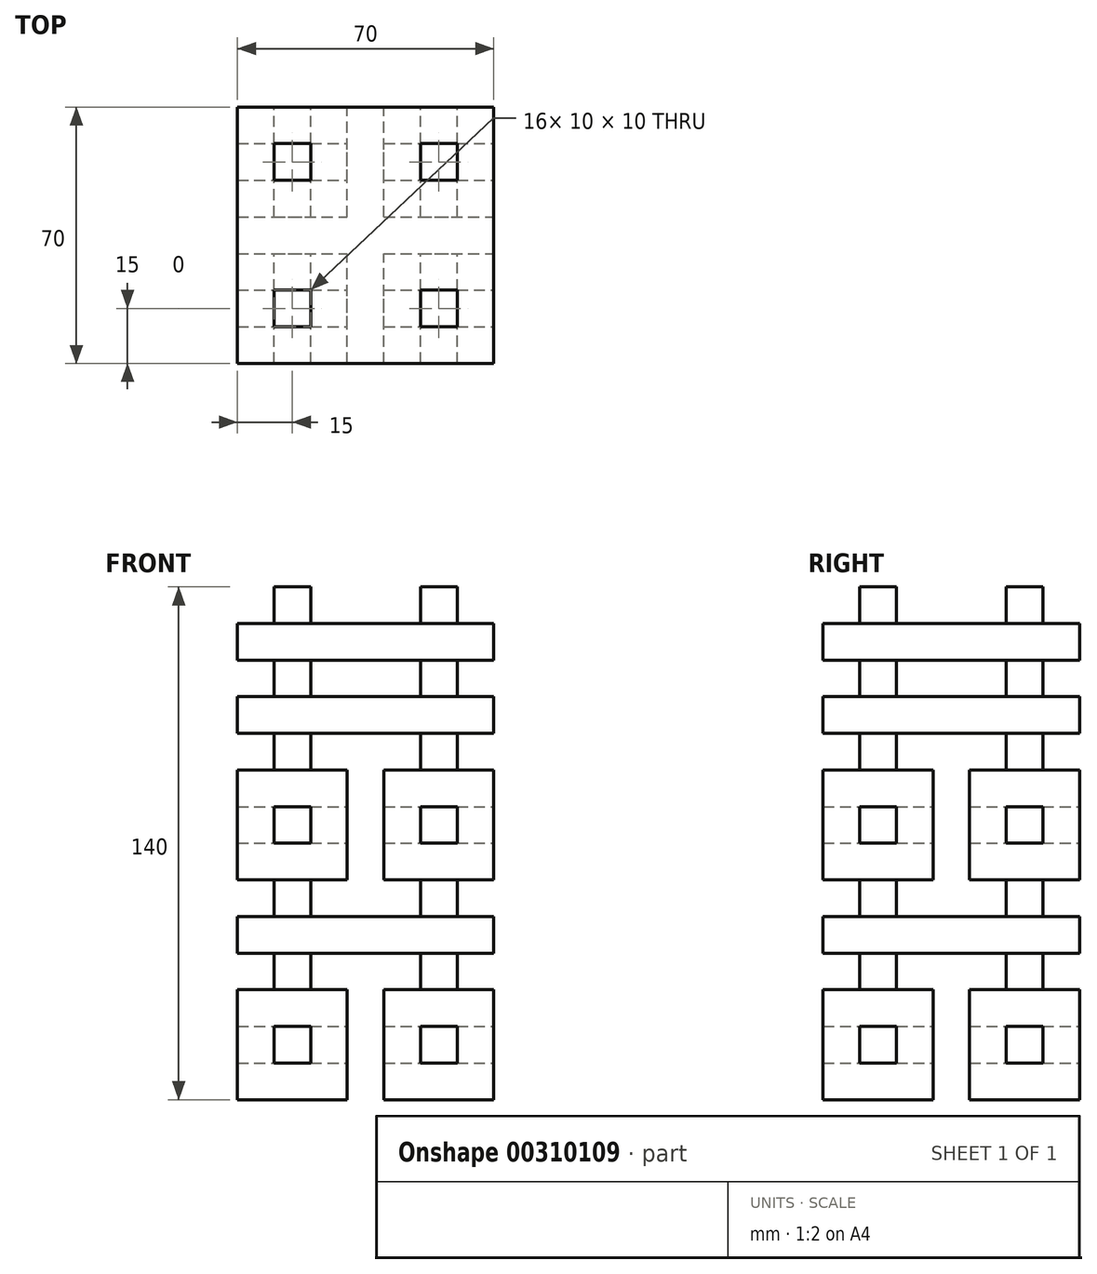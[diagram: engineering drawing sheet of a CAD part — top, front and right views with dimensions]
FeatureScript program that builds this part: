
annotation { "Feature Type Name" : "Feature", "Feature Type Description" : "" }
export const myFeature = defineFeature(function(context is Context, id is Id, definition is map)
    precondition{}
    {
        {
            var Q0;
            Q0=qCreatedBy(makeId("Front.planeOp"),FACE);
            var sketch = newSketch(context, id + "F0", { "sketchPlane" : qUnion([Q0])});
            skLineSegment(sketch, "E0.bottom", {"start": v(-25, 70) * mm, "end": v(-15, 70) * mm});
            skLineSegment(sketch, "E0.top", {"start": v(-35, -70) * mm, "end": v(-5, -70) * mm});
            skLineSegment(sketch, "E0.left", {"start": v(-35, 60) * mm, "end": v(-35, 50) * mm});
            skLineSegment(sketch, "E0.right", {"start": v(35, 60) * mm, "end": v(35, 50) * mm});
            skPoint(sketch, "E0.middle", {"position": v(0, 0) * mm});
            skLineSegment(sketch, "E1", {"start": v(-35, 60) * mm, "end": v(-25, 60) * mm});
            skLineSegment(sketch, "E2", {"start": v(-35, 50) * mm, "end": v(-25, 50) * mm});
            skLineSegment(sketch, "E3", {"start": v(-35, 40) * mm, "end": v(-25, 40) * mm});
            skLineSegment(sketch, "E4", {"start": v(-35, 20) * mm, "end": v(-25, 20) * mm});
            skLineSegment(sketch, "E5", {"start": v(-25, 10) * mm, "end": v(-15, 10) * mm});
            skLineSegment(sketch, "E6", {"start": v(-25, 0) * mm, "end": v(-15, 0) * mm});
            skLineSegment(sketch, "E7", {"start": v(-35, -10) * mm, "end": v(-25, -10) * mm});
            skLineSegment(sketch, "E8", {"start": v(-35, -20) * mm, "end": v(-25, -20) * mm});
            skLineSegment(sketch, "E9", {"start": v(-35, -30) * mm, "end": v(-25, -30) * mm});
            skLineSegment(sketch, "E10", {"start": v(-35, -40) * mm, "end": v(-25, -40) * mm});
            skLineSegment(sketch, "E11", {"start": v(-25, -50) * mm, "end": v(-15, -50) * mm});
            skLineSegment(sketch, "E12", {"start": v(-25, -60) * mm, "end": v(-15, -60) * mm});
            skLineSegment(sketch, "E13", {"start": v(-35, 30) * mm, "end": v(-25, 30) * mm});
            skLineSegment(sketch, "E14", {"start": v(-25, 70) * mm, "end": v(-25, 60) * mm});
            skLineSegment(sketch, "E15", {"start": v(-15, 70) * mm, "end": v(-15, 60) * mm});
            skLineSegment(sketch, "E16", {"start": v(-5, 20) * mm, "end": v(-5, -10) * mm});
            skLineSegment(sketch, "E17", {"start": v(5, 20) * mm, "end": v(5, -10) * mm});
            skLineSegment(sketch, "E18", {"start": v(15, 70) * mm, "end": v(15, 60) * mm});
            skLineSegment(sketch, "E19", {"start": v(25, 70) * mm, "end": v(25, 60) * mm});
            skPoint(sketch, "E20.orphan", {"position": v(-35, 70) * mm});
            skLineSegment(sketch, "E21.trimOffspring", {"start": v(-35, 40) * mm, "end": v(-35, 30) * mm});
            skLineSegment(sketch, "E22.trimOffspring", {"start": v(15, 70) * mm, "end": v(25, 70) * mm});
            skPoint(sketch, "E23.orphan", {"position": v(-5, 70) * mm});
            skPoint(sketch, "E24.orphan", {"position": v(5, 70) * mm});
            skPoint(sketch, "E25.orphan", {"position": v(35, 70) * mm});
            skLineSegment(sketch, "E26.trimOffspring", {"start": v(-25, 50) * mm, "end": v(-25, 40) * mm});
            skLineSegment(sketch, "E27.trimOffspring", {"start": v(-15, 50) * mm, "end": v(-15, 40) * mm});
            skLineSegment(sketch, "E28.trimOffspring", {"start": v(15, 50) * mm, "end": v(15, 40) * mm});
            skLineSegment(sketch, "E29.trimOffspring", {"start": v(25, 50) * mm, "end": v(25, 40) * mm});
            skLineSegment(sketch, "E30.trimOffspring", {"start": v(-15, 60) * mm, "end": v(15, 60) * mm});
            skLineSegment(sketch, "E31.trimOffspring", {"start": v(25, 60) * mm, "end": v(35, 60) * mm});
            skLineSegment(sketch, "E32.trimOffspring", {"start": v(-15, 50) * mm, "end": v(15, 50) * mm});
            skLineSegment(sketch, "E33.trimOffspring", {"start": v(25, 50) * mm, "end": v(35, 50) * mm});
            skLineSegment(sketch, "E34.trimOffspring", {"start": v(-15, 40) * mm, "end": v(15, 40) * mm});
            skLineSegment(sketch, "E35.trimOffspring", {"start": v(25, 40) * mm, "end": v(35, 40) * mm});
            skLineSegment(sketch, "E36.trimOffspring", {"start": v(-25, 30) * mm, "end": v(-25, 20) * mm});
            skLineSegment(sketch, "E37.trimOffspring", {"start": v(-15, 30) * mm, "end": v(-15, 20) * mm});
            skLineSegment(sketch, "E38.trimOffspring", {"start": v(15, 30) * mm, "end": v(15, 20) * mm});
            skLineSegment(sketch, "E39.trimOffspring", {"start": v(25, 30) * mm, "end": v(25, 20) * mm});
            skLineSegment(sketch, "E40.trimOffspring", {"start": v(-35, 20) * mm, "end": v(-35, -10) * mm});
            skLineSegment(sketch, "E41.trimOffspring", {"start": v(-15, 30) * mm, "end": v(15, 30) * mm});
            skLineSegment(sketch, "E42.trimOffspring", {"start": v(25, 30) * mm, "end": v(35, 30) * mm});
            skLineSegment(sketch, "E43.trimOffspring", {"start": v(35, 20) * mm, "end": v(35, -10) * mm});
            skLineSegment(sketch, "E44.trimOffspring", {"start": v(-15, 20) * mm, "end": v(-5, 20) * mm});
            skLineSegment(sketch, "E45.trimOffspring", {"start": v(25, 20) * mm, "end": v(35, 20) * mm});
            skLineSegment(sketch, "E46.trimOffspring", {"start": v(-25, 10) * mm, "end": v(-25, 0) * mm});
            skLineSegment(sketch, "E47.trimOffspring", {"start": v(-15, 10) * mm, "end": v(-15, 0) * mm});
            skLineSegment(sketch, "E48.trimOffspring", {"start": v(15, 10) * mm, "end": v(25, 10) * mm});
            skPoint(sketch, "E49.orphan", {"position": v(-35, 10) * mm});
            skPoint(sketch, "E50.orphan", {"position": v(-35, 0) * mm});
            skLineSegment(sketch, "E51.trimOffspring", {"start": v(-25, -10) * mm, "end": v(-25, -20) * mm});
            skLineSegment(sketch, "E52.trimOffspring", {"start": v(-15, -10) * mm, "end": v(-15, -20) * mm});
            skLineSegment(sketch, "E53.trimOffspring", {"start": v(5, 20) * mm, "end": v(15, 20) * mm});
            skLineSegment(sketch, "E54.trimOffspring", {"start": v(15, 0) * mm, "end": v(25, 0) * mm});
            skLineSegment(sketch, "E55.trimOffspring", {"start": v(5, -10) * mm, "end": v(15, -10) * mm});
            skLineSegment(sketch, "E56.trimOffspring", {"start": v(25, 10) * mm, "end": v(25, 0) * mm});
            skLineSegment(sketch, "E57.trimOffspring", {"start": v(15, 10) * mm, "end": v(15, 0) * mm});
            skLineSegment(sketch, "E58.trimOffspring", {"start": v(15, -10) * mm, "end": v(15, -20) * mm});
            skLineSegment(sketch, "E59.trimOffspring", {"start": v(25, -10) * mm, "end": v(25, -20) * mm});
            skLineSegment(sketch, "E60.trimOffspring", {"start": v(-35, -20) * mm, "end": v(-35, -30) * mm});
            skLineSegment(sketch, "E61.trimOffspring", {"start": v(-5, -40) * mm, "end": v(-5, -70) * mm});
            skLineSegment(sketch, "E62.trimOffspring", {"start": v(-15, -10) * mm, "end": v(-5, -10) * mm});
            skLineSegment(sketch, "E63.trimOffspring", {"start": v(25, -10) * mm, "end": v(35, -10) * mm});
            skLineSegment(sketch, "E64.trimOffspring", {"start": v(5, -40) * mm, "end": v(5, -70) * mm});
            skLineSegment(sketch, "E65.trimOffspring", {"start": v(35, -20) * mm, "end": v(35, -30) * mm});
            skLineSegment(sketch, "E66.trimOffspring", {"start": v(-15, -20) * mm, "end": v(15, -20) * mm});
            skLineSegment(sketch, "E67.trimOffspring", {"start": v(25, -20) * mm, "end": v(35, -20) * mm});
            skLineSegment(sketch, "E68.trimOffspring", {"start": v(-35, -40) * mm, "end": v(-35, -70) * mm});
            skLineSegment(sketch, "E69.trimOffspring", {"start": v(-25, -30) * mm, "end": v(-25, -40) * mm});
            skLineSegment(sketch, "E70.trimOffspring", {"start": v(-15, -30) * mm, "end": v(-15, -40) * mm});
            skLineSegment(sketch, "E71.trimOffspring", {"start": v(15, -30) * mm, "end": v(15, -40) * mm});
            skLineSegment(sketch, "E72.trimOffspring", {"start": v(25, -30) * mm, "end": v(25, -40) * mm});
            skLineSegment(sketch, "E73.trimOffspring", {"start": v(35, 40) * mm, "end": v(35, 30) * mm});
            skLineSegment(sketch, "E74.trimOffspring", {"start": v(35, -40) * mm, "end": v(35, -70) * mm});
            skLineSegment(sketch, "E75.trimOffspring", {"start": v(5, -40) * mm, "end": v(15, -40) * mm});
            skLineSegment(sketch, "E76.trimOffspring", {"start": v(15, -50) * mm, "end": v(25, -50) * mm});
            skLineSegment(sketch, "E77.trimOffspring", {"start": v(15, -60) * mm, "end": v(25, -60) * mm});
            skLineSegment(sketch, "E78.trimOffspring", {"start": v(5, -70) * mm, "end": v(35, -70) * mm});
            skLineSegment(sketch, "E79.trimOffspring", {"start": v(-25, -50) * mm, "end": v(-25, -60) * mm});
            skLineSegment(sketch, "E80.trimOffspring", {"start": v(-15, -50) * mm, "end": v(-15, -60) * mm});
            skPoint(sketch, "E81.orphan", {"position": v(-35, -60) * mm});
            skPoint(sketch, "E82.orphan", {"position": v(-35, -50) * mm});
            skLineSegment(sketch, "E83.trimOffspring", {"start": v(25, -50) * mm, "end": v(25, -60) * mm});
            skLineSegment(sketch, "E84.trimOffspring", {"start": v(15, -50) * mm, "end": v(15, -60) * mm});
            skLineSegment(sketch, "E85.trimOffspring", {"start": v(25, -40) * mm, "end": v(35, -40) * mm});
            skLineSegment(sketch, "E86.trimOffspring", {"start": v(-15, -40) * mm, "end": v(-5, -40) * mm});
            skLineSegment(sketch, "E87.trimOffspring", {"start": v(-15, -30) * mm, "end": v(15, -30) * mm});
            skLineSegment(sketch, "E88.trimOffspring", {"start": v(25, -30) * mm, "end": v(35, -30) * mm});
            skSolve(sketch);
        }
        {
            var Q0;
            Q0 = qSketchRegion(id + "F0", true);
            extrude(context, id + "F1", {"entities" : qUnion([Q0]), "depth" : 70 * mm});
        }
        {
            var Q0;
            Q0=makeQuery(id+"F1.opExtrude","SWEPT_FACE",FACE,{"disambiguationData":[OSD([sQuery(id+"F0.wireOp",EDGE,"E74.trimOffspring")])]});
            var sketch = newSketch(context, id + "F2", { "sketchPlane" : qUnion([Q0])});
            skLineSegment(sketch, "E89", {"start": v(-70, 70) * mm, "end": v(-60, 70) * mm});
            skLineSegment(sketch, "E90", {"start": v(0, 70) * mm, "end": v(0, 60) * mm});
            skLineSegment(sketch, "E91", {"start": v(-30, -70) * mm, "end": v(-40, -70) * mm});
            skLineSegment(sketch, "E92", {"start": v(0, 60) * mm, "end": v(-10, 60) * mm});
            skLineSegment(sketch, "E93", {"start": v(0, 50) * mm, "end": v(-10, 50) * mm});
            skLineSegment(sketch, "E94", {"start": v(-70, 40) * mm, "end": v(-60, 40) * mm});
            skLineSegment(sketch, "E95", {"start": v(-70, 30) * mm, "end": v(-60, 30) * mm});
            skLineSegment(sketch, "E96", {"start": v(-70, 20) * mm, "end": v(-60, 20) * mm});
            skLineSegment(sketch, "E97", {"start": v(-60, 10) * mm, "end": v(-50, 10) * mm});
            skLineSegment(sketch, "E98", {"start": v(-70, -20) * mm, "end": v(-60, -20) * mm});
            skLineSegment(sketch, "E99", {"start": v(-70, -30) * mm, "end": v(-60, -30) * mm});
            skLineSegment(sketch, "E100", {"start": v(-70, -40) * mm, "end": v(-60, -40) * mm});
            skLineSegment(sketch, "E101", {"start": v(-60, 70) * mm, "end": v(-60, 60) * mm});
            skLineSegment(sketch, "E102", {"start": v(-50, 70) * mm, "end": v(-50, 60) * mm});
            skLineSegment(sketch, "E103", {"start": v(-20, 70) * mm, "end": v(-20, 60) * mm});
            skLineSegment(sketch, "E104", {"start": v(-10, 70) * mm, "end": v(-10, 60) * mm});
            skLineSegment(sketch, "E105", {"start": v(-60, 0) * mm, "end": v(-50, 0) * mm});
            skLineSegment(sketch, "E106", {"start": v(-60, -50) * mm, "end": v(-50, -50) * mm});
            skLineSegment(sketch, "E107", {"start": v(-60, -60) * mm, "end": v(-50, -60) * mm});
            skLineSegment(sketch, "E108", {"start": v(-70, -10) * mm, "end": v(-60, -10) * mm});
            skLineSegment(sketch, "E109.trimOffspring", {"start": v(-50, 70) * mm, "end": v(-20, 70) * mm});
            skLineSegment(sketch, "E110.trimOffspring", {"start": v(-70, 60) * mm, "end": v(-70, 70) * mm});
            skLineSegment(sketch, "E111.trimOffspring", {"start": v(-60, 50) * mm, "end": v(-60, 40) * mm});
            skLineSegment(sketch, "E112.trimOffspring", {"start": v(-50, 50) * mm, "end": v(-50, 40) * mm});
            skLineSegment(sketch, "E113.trimOffspring", {"start": v(-20, 50) * mm, "end": v(-20, 40) * mm});
            skLineSegment(sketch, "E114.trimOffspring", {"start": v(-10, 50) * mm, "end": v(-10, 40) * mm});
            skLineSegment(sketch, "E115.trimOffspring", {"start": v(0, 50) * mm, "end": v(0, 40) * mm});
            skLineSegment(sketch, "E116.trimOffspring", {"start": v(-60, 60) * mm, "end": v(-70, 60) * mm});
            skLineSegment(sketch, "E117.trimOffspring", {"start": v(-10, 70) * mm, "end": v(0, 70) * mm});
            skLineSegment(sketch, "E118.trimOffspring", {"start": v(-20, 60) * mm, "end": v(-50, 60) * mm});
            skPoint(sketch, "E119.start.orphan", {"position": v(-40, 70) * mm});
            skPoint(sketch, "E120.start.orphan", {"position": v(-30, 70) * mm});
            skLineSegment(sketch, "E121.trimOffspring", {"start": v(-60, 50) * mm, "end": v(-70, 50) * mm});
            skLineSegment(sketch, "E122.trimOffspring", {"start": v(-50, 40) * mm, "end": v(-20, 40) * mm});
            skLineSegment(sketch, "E123.trimOffspring", {"start": v(-70, 40) * mm, "end": v(-70, 50) * mm});
            skLineSegment(sketch, "E124.trimOffspring", {"start": v(-60, 30) * mm, "end": v(-60, 20) * mm});
            skLineSegment(sketch, "E125.trimOffspring", {"start": v(-50, 30) * mm, "end": v(-50, 20) * mm});
            skLineSegment(sketch, "E126.trimOffspring", {"start": v(-40, 20) * mm, "end": v(-40, -10) * mm});
            skLineSegment(sketch, "E127.trimOffspring", {"start": v(-30, 20) * mm, "end": v(-30, -10) * mm});
            skLineSegment(sketch, "E128.trimOffspring", {"start": v(-20, 30) * mm, "end": v(-20, 20) * mm});
            skLineSegment(sketch, "E129.trimOffspring", {"start": v(-10, 30) * mm, "end": v(-10, 20) * mm});
            skLineSegment(sketch, "E130.trimOffspring", {"start": v(0, 30) * mm, "end": v(0, 20) * mm});
            skLineSegment(sketch, "E131.trimOffspring", {"start": v(-20, 50) * mm, "end": v(-50, 50) * mm});
            skLineSegment(sketch, "E132.trimOffspring", {"start": v(-10, 40) * mm, "end": v(0, 40) * mm});
            skLineSegment(sketch, "E133.trimOffspring", {"start": v(-50, 30) * mm, "end": v(-20, 30) * mm});
            skLineSegment(sketch, "E134.trimOffspring", {"start": v(-50, 20) * mm, "end": v(-40, 20) * mm});
            skLineSegment(sketch, "E135.trimOffspring", {"start": v(-70, 20) * mm, "end": v(-70, 30) * mm});
            skLineSegment(sketch, "E136.trimOffspring", {"start": v(-10, 30) * mm, "end": v(0, 30) * mm});
            skLineSegment(sketch, "E137.trimOffspring", {"start": v(-10, 20) * mm, "end": v(0, 20) * mm});
            skLineSegment(sketch, "E138.trimOffspring", {"start": v(-60, 10) * mm, "end": v(-60, 0) * mm});
            skLineSegment(sketch, "E139.trimOffspring", {"start": v(-50, 10) * mm, "end": v(-50, 0) * mm});
            skLineSegment(sketch, "E140.trimOffspring", {"start": v(-30, 20) * mm, "end": v(-20, 20) * mm});
            skLineSegment(sketch, "E141.trimOffspring", {"start": v(-20, 10) * mm, "end": v(-20, 0) * mm});
            skLineSegment(sketch, "E142.trimOffspring", {"start": v(-10, 10) * mm, "end": v(-10, 0) * mm});
            skLineSegment(sketch, "E143.trimOffspring", {"start": v(-20, 10) * mm, "end": v(-10, 10) * mm});
            skLineSegment(sketch, "E144.trimOffspring", {"start": v(-20, 0) * mm, "end": v(-10, 0) * mm});
            skLineSegment(sketch, "E145.trimOffspring", {"start": v(-50, -10) * mm, "end": v(-50, -20) * mm});
            skLineSegment(sketch, "E146.trimOffspring", {"start": v(-60, -10) * mm, "end": v(-60, -20) * mm});
            skPoint(sketch, "E147.orphan", {"position": v(-70, 10) * mm});
            skPoint(sketch, "E148.orphan", {"position": v(-70, 0) * mm});
            skLineSegment(sketch, "E149.trimOffspring", {"start": v(-20, -10) * mm, "end": v(-20, -20) * mm});
            skLineSegment(sketch, "E150.trimOffspring", {"start": v(-10, -10) * mm, "end": v(-10, -20) * mm});
            skLineSegment(sketch, "E151.trimOffspring", {"start": v(0, -10) * mm, "end": v(0, -20) * mm});
            skLineSegment(sketch, "E152.trimOffspring", {"start": v(-50, -10) * mm, "end": v(-40, -10) * mm});
            skLineSegment(sketch, "E153.trimOffspring", {"start": v(-50, -20) * mm, "end": v(-20, -20) * mm});
            skLineSegment(sketch, "E154.trimOffspring", {"start": v(-30, -10) * mm, "end": v(-20, -10) * mm});
            skLineSegment(sketch, "E155.trimOffspring", {"start": v(-40, -40) * mm, "end": v(-40, -70) * mm});
            skLineSegment(sketch, "E156.trimOffspring", {"start": v(-30, -40) * mm, "end": v(-30, -70) * mm});
            skLineSegment(sketch, "E157.trimOffspring", {"start": v(-10, -10) * mm, "end": v(0, -10) * mm});
            skLineSegment(sketch, "E158.trimOffspring", {"start": v(-10, -20) * mm, "end": v(0, -20) * mm});
            skLineSegment(sketch, "E159.trimOffspring", {"start": v(-70, -20) * mm, "end": v(-70, -10) * mm});
            skLineSegment(sketch, "E160.trimOffspring", {"start": v(-60, -30) * mm, "end": v(-60, -40) * mm});
            skLineSegment(sketch, "E161.trimOffspring", {"start": v(-50, -30) * mm, "end": v(-50, -40) * mm});
            skLineSegment(sketch, "E162.trimOffspring", {"start": v(-20, -30) * mm, "end": v(-20, -40) * mm});
            skLineSegment(sketch, "E163.trimOffspring", {"start": v(-10, -30) * mm, "end": v(-10, -40) * mm});
            skLineSegment(sketch, "E164.trimOffspring", {"start": v(0, -30) * mm, "end": v(0, -40) * mm});
            skLineSegment(sketch, "E165.trimOffspring", {"start": v(-50, -30) * mm, "end": v(-20, -30) * mm});
            skLineSegment(sketch, "E166.trimOffspring", {"start": v(-50, -40) * mm, "end": v(-40, -40) * mm});
            skLineSegment(sketch, "E167.trimOffspring", {"start": v(-60, -50) * mm, "end": v(-60, -60) * mm});
            skLineSegment(sketch, "E168.trimOffspring", {"start": v(-70, -40) * mm, "end": v(-70, -30) * mm});
            skPoint(sketch, "E169.orphan", {"position": v(-70, -50) * mm});
            skPoint(sketch, "E170.end.orphan", {"position": v(-70, -60) * mm});
            skPoint(sketch, "E171.orphan", {"position": v(-70, -70) * mm});
            skLineSegment(sketch, "E172.trimOffspring", {"start": v(-50, -50) * mm, "end": v(-50, -60) * mm});
            skLineSegment(sketch, "E173.trimOffspring", {"start": v(-10, -50) * mm, "end": v(-10, -60) * mm});
            skLineSegment(sketch, "E174.trimOffspring", {"start": v(-20, -50) * mm, "end": v(-20, -60) * mm});
            skLineSegment(sketch, "E175.trimOffspring", {"start": v(-20, -50) * mm, "end": v(-10, -50) * mm});
            skLineSegment(sketch, "E176.trimOffspring", {"start": v(-20, -60) * mm, "end": v(-10, -60) * mm});
            skPoint(sketch, "E177.orphan", {"position": v(0, -50) * mm});
            skPoint(sketch, "E178.orphan", {"position": v(0, -60) * mm});
            skLineSegment(sketch, "E179.trimOffspring", {"start": v(-30, -40) * mm, "end": v(-20, -40) * mm});
            skLineSegment(sketch, "E180.trimOffspring", {"start": v(-10, -40) * mm, "end": v(0, -40) * mm});
            skLineSegment(sketch, "E181.trimOffspring", {"start": v(-10, -30) * mm, "end": v(0, -30) * mm});
            skSolve(sketch);
        }
        {
            var Q0;
            Q0=makeQuery(id+"F2.imprint","IMPRINT",FACE,{"disambiguationData":[TD([[makeQuery(id+"F2.imprint","IMPRINT",EDGE,{"derivedFrom":sQuery(id+"F2.wireOp",EDGE,"E125.trimOffspring")}),1.0]])]});
            var Q1;
            Q1=makeQuery(id+"F2.imprint","IMPRINT",FACE,{"disambiguationData":[TD([[makeQuery(id+"F2.imprint","IMPRINT",EDGE,{"derivedFrom":sQuery(id+"F2.wireOp",EDGE,"E150.trimOffspring")}),1.0]])]});
            var Q2;
            Q2=makeQuery(id+"F2.imprint","IMPRINT",FACE,{"disambiguationData":[TD([[makeQuery(id+"F2.imprint","IMPRINT",EDGE,{"derivedFrom":sQuery(id+"F2.wireOp",EDGE,"E141.trimOffspring")}),1.0]])]});
            var Q3;
            Q3=makeQuery(id+"F2.imprint","IMPRINT",FACE,{"disambiguationData":[TD([[makeQuery(id+"F2.imprint","IMPRINT",EDGE,{"derivedFrom":sQuery(id+"F2.wireOp",EDGE,"E97")}),-1.0]])]});
            var Q4;
            Q4=makeQuery(id+"F2.imprint","IMPRINT",FACE,{"disambiguationData":[TD([[makeQuery(id+"F2.imprint","IMPRINT",EDGE,{"derivedFrom":sQuery(id+"F2.wireOp",EDGE,"E95")}),-1.0]])]});
            var Q5;
            Q5=makeQuery(id+"F2.imprint","IMPRINT",FACE,{"disambiguationData":[TD([[makeQuery(id+"F2.imprint","IMPRINT",EDGE,{"derivedFrom":sQuery(id+"F2.wireOp",EDGE,"E129.trimOffspring")}),1.0]])]});
            var Q6;
            Q6=makeQuery(id+"F2.imprint","IMPRINT",FACE,{"disambiguationData":[TD([[makeQuery(id+"F2.imprint","IMPRINT",EDGE,{"derivedFrom":sQuery(id+"F2.wireOp",EDGE,"E93")}),1.0]])]});
            var Q7;
            Q7=makeQuery(id+"F2.imprint","IMPRINT",FACE,{"disambiguationData":[TD([[makeQuery(id+"F2.imprint","IMPRINT",EDGE,{"derivedFrom":sQuery(id+"F2.wireOp",EDGE,"E112.trimOffspring")}),1.0]])]});
            var Q8;
            Q8=makeQuery(id+"F2.imprint","IMPRINT",FACE,{"disambiguationData":[TD([[makeQuery(id+"F2.imprint","IMPRINT",EDGE,{"derivedFrom":sQuery(id+"F2.wireOp",EDGE,"E94")}),1.0]])]});
            var Q9;
            Q9=makeQuery(id+"F2.imprint","IMPRINT",FACE,{"disambiguationData":[TD([[makeQuery(id+"F2.imprint","IMPRINT",EDGE,{"derivedFrom":sQuery(id+"F2.wireOp",EDGE,"E89")}),-1.0]])]});
            var Q10;
            Q10=makeQuery(id+"F2.imprint","IMPRINT",FACE,{"disambiguationData":[TD([[makeQuery(id+"F2.imprint","IMPRINT",EDGE,{"derivedFrom":sQuery(id+"F2.wireOp",EDGE,"E102")}),1.0]])]});
            var Q11;
            Q11=makeQuery(id+"F2.imprint","IMPRINT",FACE,{"disambiguationData":[TD([[makeQuery(id+"F2.imprint","IMPRINT",EDGE,{"derivedFrom":sQuery(id+"F2.wireOp",EDGE,"E90")}),-1.0]])]});
            var Q12;
            Q12=makeQuery(id+"F2.imprint","IMPRINT",FACE,{"disambiguationData":[TD([[makeQuery(id+"F2.imprint","IMPRINT",EDGE,{"derivedFrom":sQuery(id+"F2.wireOp",EDGE,"E98")}),1.0]])]});
            var Q13;
            Q13=makeQuery(id+"F2.imprint","IMPRINT",FACE,{"disambiguationData":[TD([[makeQuery(id+"F2.imprint","IMPRINT",EDGE,{"derivedFrom":sQuery(id+"F2.wireOp",EDGE,"E99")}),-1.0]])]});
            var Q14;
            Q14=makeQuery(id+"F2.imprint","IMPRINT",FACE,{"disambiguationData":[TD([[makeQuery(id+"F2.imprint","IMPRINT",EDGE,{"derivedFrom":sQuery(id+"F2.wireOp",EDGE,"E161.trimOffspring")}),1.0]])]});
            var Q15;
            Q15=makeQuery(id+"F2.imprint","IMPRINT",FACE,{"disambiguationData":[TD([[makeQuery(id+"F2.imprint","IMPRINT",EDGE,{"derivedFrom":sQuery(id+"F2.wireOp",EDGE,"E163.trimOffspring")}),1.0]])]});
            var Q16;
            Q16=makeQuery(id+"F2.imprint","IMPRINT",FACE,{"disambiguationData":[TD([[makeQuery(id+"F2.imprint","IMPRINT",EDGE,{"derivedFrom":sQuery(id+"F2.wireOp",EDGE,"E173.trimOffspring")}),-1.0]])]});
            var Q17;
            Q17=makeQuery(id+"F2.imprint","IMPRINT",FACE,{"disambiguationData":[TD([[makeQuery(id+"F2.imprint","IMPRINT",EDGE,{"derivedFrom":sQuery(id+"F2.wireOp",EDGE,"E106")}),-1.0]])]});
            var Q18;
            Q18=makeQuery(id+"F2.imprint","IMPRINT",FACE,{"disambiguationData":[TD([[makeQuery(id+"F2.imprint","IMPRINT",EDGE,{"derivedFrom":sQuery(id+"F2.wireOp",EDGE,"E91")}),1.0]])]});
            extrude(context, id + "F3", {"entities" : qUnion([Q0, Q1, Q2, Q3, Q4, Q5, Q6, Q7, Q8, Q9, Q10, Q11, Q12, Q13, Q14, Q15, Q16, Q17, Q18]), "operationType" : NewBodyOperationType.REMOVE, "oppositeDirection" : true, "depth" : 100 * mm});
        }
    });
